# Revit family: xPump_Residential-Grinder-Zoeller-803_805_807_Automatic_Series
name_source: partatom
category: Mechanical Equipment
revit_build: Autodesk Revit 2014 (Build: 20130308_1515(x64)
units: mm (PartAtom-declared; Revit-internal decimal feet)

## types (6) — shared parameters
Assembly Code = D2010900
Cooling = Oil Filled
Cord Length = 15 ft.
Cord Type = UL-listed, 3-wire plug
Default Elevation = 0"
Description = Shark® 803/805/807 Residential Grinders. Fractional HP grinder pumps.
Discharge Diameter = 1 1/4" NPT
Discharge Height = 4 15/16"
Discharge Radius = 5/8"
Height = 17 1/4"
Hertz = 60
Impeller Type = Non-clogging vortex
Installation Type = Floor Mounted
Insulation = Class B
Length = 8 29/32"
Manufacturer = Zoeller
Material = Cast Iron-Zoeller-Powder Coated Epoxy
Max. Water Temp. = 130 °F
Mechanical Seals = Carbon and Ceramic
Model = 803
Motor Protection = Automatic thermal overload
Off Point = 5-3/4
On Point = 13
Operation = Automatic
Phase = 1
Price = Prices may vary. Please consult Manufacturer Representative for most up-to-date price list.
Product Documentation Link = http://cdn.qleapahead.com
Product Page URL = http://www.zoellerpumps.com
RPM = 3400 RPM
Shipping Weight = 65.00 lb
Type = Capacitor start/capacitor run
URL = http://www.zoellerpumps.com
Warranty Information = 36 Months (Limited)
Waste Connection = Yes

## per-type parameters (varying)
| type | Amps | Apparent Load | Max. Flow at Min. Head | Max. Head | Motor | Voltage | Width |
| M803 | 7 A | 805 VA | 35 GPM @ 5' | 35 ft. | 1/2 HP | 115 V | 7 21/32" |
| D803 | 3 A | 690 VA | 35 GPM @ 5' | 35 ft. | 1/2 HP | 230 V | 11 11/32" |
| M805 | 9 A | 1035 VA | 40 GPM @ 5' | 45 ft. | 3/4 HP | 115 V | 7 21/32" |
| D805 | 4 A | 920 VA | 40 GPM @ 5' | 45 ft. | 3/4 HP | 230 V | 7 21/32" |
| M807 | 11 A | 1265 VA | 45 GPM @ 5' | 55 ft. | 1 HP | 115 V | 7 21/32" |
| D807 | 5 A | 1150 VA | 45 GPM @ 5' | 55 ft. | 1 HP | 230 V | 7 21/32" |

## geometry (parser evidence)
native form markers: Sweep x2
no freeform markers — native parametric forms only
